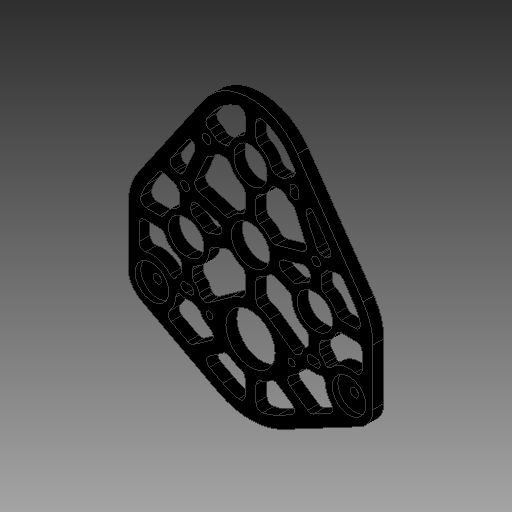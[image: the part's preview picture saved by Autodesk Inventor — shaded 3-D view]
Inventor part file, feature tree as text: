
AUTODESK INVENTOR PART (.ipt)
format: ipt  version: 2019 (Build 230136000, 136)  size: 517,632 bytes
history: native  units: in
note: dims shown in document units (in); Inventor stores cm internally (conversion verified against a paired STEP export)
features: fillet x1
ambient origin geometry x8: Origin, YZ Plane, XZ Plane, XY Plane, X Axis, Y Axis, Z Axis, Center Point
bodies: Solid1 (feature_tree)
feature tree (1):
  fillet  "Fillet68"  [1 undecoded]
note: 1 required parameter value undecoded (feature->parameter linkage not recoverable at this tier; creation-order binding heuristic only, values carry confidence <= 0.55)
